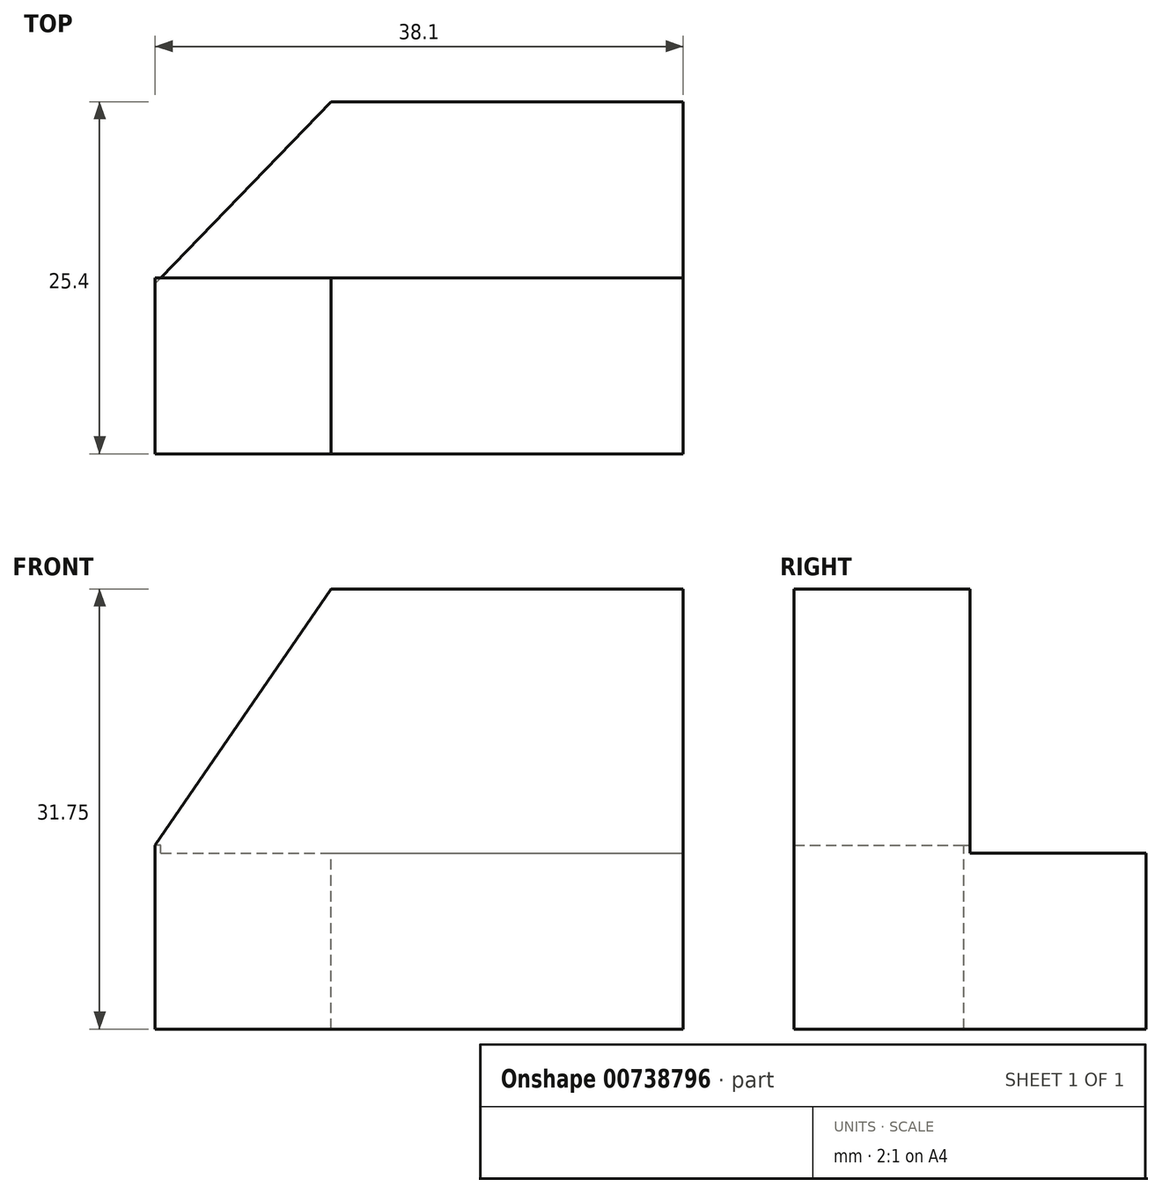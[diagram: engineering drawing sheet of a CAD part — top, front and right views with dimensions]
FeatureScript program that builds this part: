
annotation { "Feature Type Name" : "Feature", "Feature Type Description" : "" }
export const myFeature = defineFeature(function(context is Context, id is Id, definition is map)
    precondition{}
    {
        {
            var Q0;
            Q0=qCreatedBy(makeId("Front.planeOp"),FACE);
            var sketch = newSketch(context, id + "F0", { "sketchPlane" : qUnion([Q0])});
            skLineSegment(sketch, "E0", {"start": v(-22.16, 18.48) * mm, "end": v(-22.16, -13.27) * mm});
            skLineSegment(sketch, "E1", {"start": v(-22.16, -13.27) * mm, "end": v(15.94, -13.27) * mm});
            skLineSegment(sketch, "E2", {"start": v(15.94, -13.27) * mm, "end": v(15.94, 18.48) * mm});
            skLineSegment(sketch, "E3", {"start": v(15.94, 18.48) * mm, "end": v(-22.16, 18.48) * mm});
            skSolve(sketch);
        }
        {
            var Q0;
            Q0=makeQuery(id+"F0.imprint","IMPRINT",FACE,{"disambiguationData":[TD([[makeQuery(id+"F0.imprint","IMPRINT",EDGE,{"derivedFrom":sQuery(id+"F0.wireOp",EDGE,"E0")}),1.0]])]});
            extrude(context, id + "F1", {"entities" : qUnion([Q0]), "depth" : 25.4 * mm, "offsetDistance" : 25.4 * mm});
        }
        {
            var Q0;
            Q0=qCreatedBy(makeId("Front.planeOp"),FACE);
            var sketch = newSketch(context, id + "F2", { "sketchPlane" : qUnion([Q0])});
            skLineSegment(sketch, "E4", {"start": v(-22.16, -0.57) * mm, "end": v(15.94, -0.57) * mm});
            skLineSegment(sketch, "E5", {"start": v(-22.16, -0.57) * mm, "end": v(-22.16, 18.6) * mm});
            skLineSegment(sketch, "E6", {"start": v(-22.16, 18.6) * mm, "end": v(15.98, 18.6) * mm});
            skLineSegment(sketch, "E7", {"start": v(15.98, 18.6) * mm, "end": v(15.94, -0.57) * mm});
            skSolve(sketch);
        }
        {
            var Q0;
            Q0=qSketchRegion(id+"F2",true);
            extrude(context, id + "F3", {"entities" : qUnion([Q0]), "operationType" : NewBodyOperationType.REMOVE, "depth" : 12.7 * mm, "offsetDistance" : 25.4 * mm});
        }
        {
            var Q0;
            Q0=qCreatedBy(makeId("Top.planeOp"),FACE);
            var sketch = newSketch(context, id + "F4", { "sketchPlane" : qUnion([Q0])});
            skLineSegment(sketch, "E8", {"start": v(-22.16, -13.14) * mm, "end": v(-9.46, 0) * mm});
            skLineSegment(sketch, "E9", {"start": v(-9.46, 0) * mm, "end": v(-22.21, 0) * mm});
            skLineSegment(sketch, "E10", {"start": v(-22.21, 0) * mm, "end": v(-22.16, -13.14) * mm});
            skSolve(sketch);
        }
        {
            var Q0;
            Q0=qSketchRegion(id+"F4",true);
            extrude(context, id + "F5", {"entities" : qUnion([Q0]), "operationType" : NewBodyOperationType.REMOVE, "endBound" : BoundingType.THROUGH_ALL, "oppositeDirection" : true, "depth" : 25.4 * mm, "offsetDistance" : 25.4 * mm});
        }
        {
            var Q0;
            Q0=qCreatedBy(makeId("Front.planeOp"),FACE);
            var sketch = newSketch(context, id + "F6", { "sketchPlane" : qUnion([Q0])});
            skLineSegment(sketch, "E11", {"start": v(-9.46, 18.48) * mm, "end": v(-22.16, 0) * mm});
            skLineSegment(sketch, "E12", {"start": v(-22.16, 0) * mm, "end": v(-22.16, 18.48) * mm});
            skLineSegment(sketch, "E13", {"start": v(-22.16, 18.48) * mm, "end": v(-9.46, 18.48) * mm});
            skSolve(sketch);
        }
        {
            var Q0;
            Q0=qSketchRegion(id+"F6",true);
            extrude(context, id + "F7", {"entities" : qUnion([Q0]), "operationType" : NewBodyOperationType.REMOVE, "depth" : 44.7 * mm, "offsetDistance" : 25.4 * mm});
        }
    });
